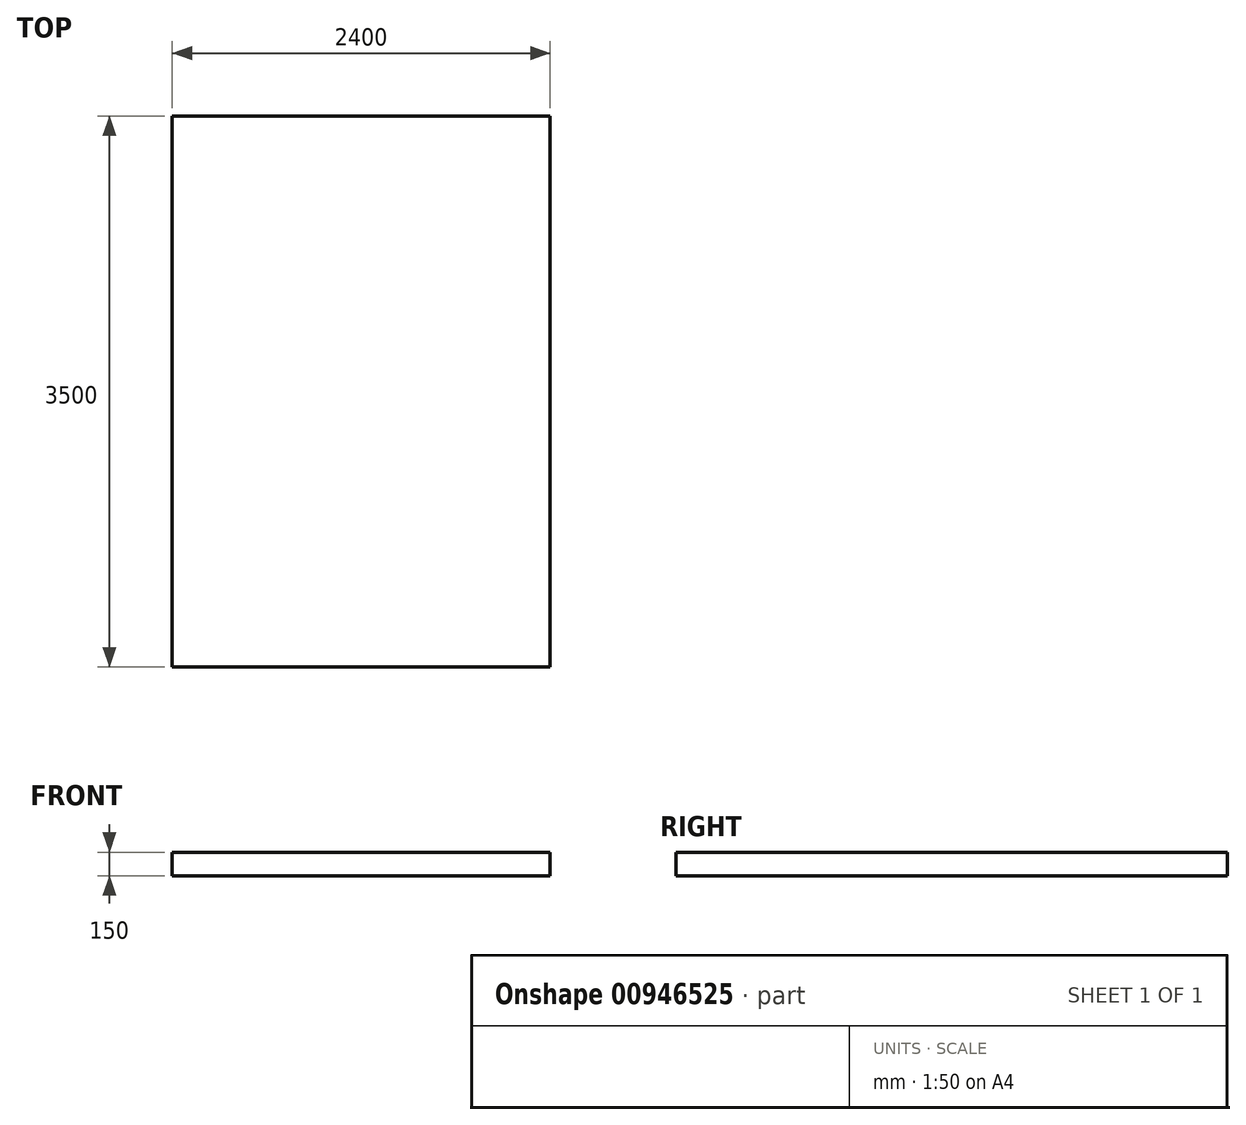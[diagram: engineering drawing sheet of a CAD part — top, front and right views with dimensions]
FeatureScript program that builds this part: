
annotation { "Feature Type Name" : "Feature", "Feature Type Description" : "" }
export const myFeature = defineFeature(function(context is Context, id is Id, definition is map)
    precondition{}
    {
        {
            var Q0;
            Q0=qCreatedBy(makeId("Front.planeOp"),FACE);
            var sketch = newSketch(context, id + "F0", { "sketchPlane" : qUnion([Q0])});
            skLineSegment(sketch, "E0.bottom", {"start": v(0, 0) * mm, "end": v(2400, 0) * mm});
            skLineSegment(sketch, "E0.top", {"start": v(0, 150) * mm, "end": v(2400, 150) * mm});
            skLineSegment(sketch, "E0.left", {"start": v(0, 0) * mm, "end": v(0, 150) * mm});
            skLineSegment(sketch, "E0.right", {"start": v(2400, 0) * mm, "end": v(2400, 150) * mm});
            skSolve(sketch);
        }
        {
            var Q0;
            Q0 = qSketchRegion(id + "F0", true);
            extrude(context, id + "F1", {"entities" : qUnion([Q0]), "oppositeDirection" : true, "depth" : 3500 * mm, "offsetDistance" : 25 * mm});
        }
    });
